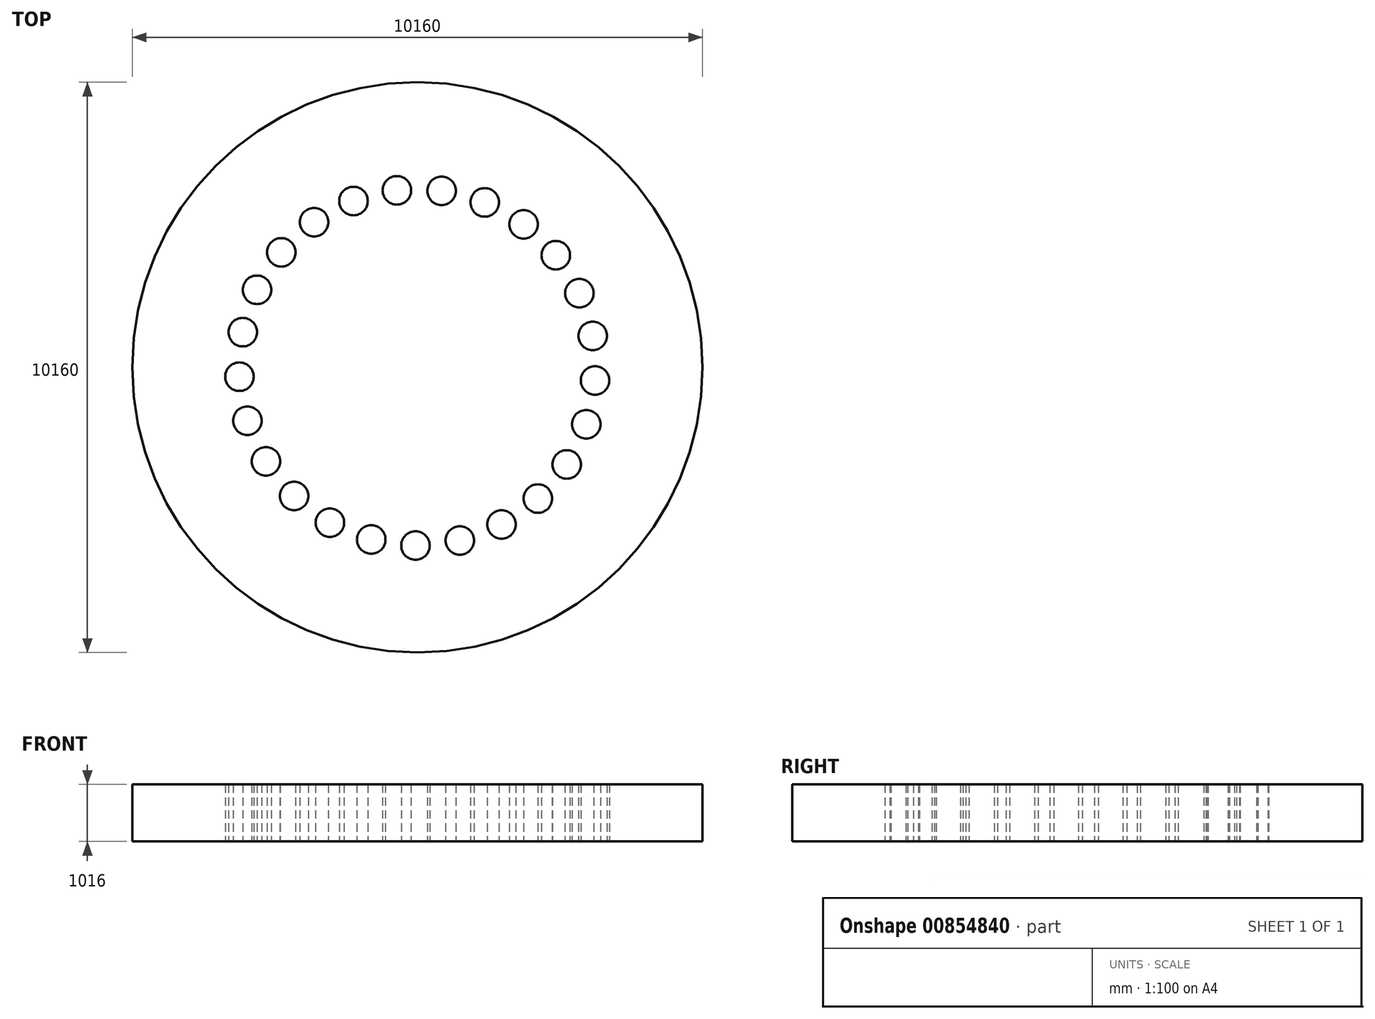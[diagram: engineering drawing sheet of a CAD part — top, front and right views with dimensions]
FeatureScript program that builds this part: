
annotation { "Feature Type Name" : "Feature", "Feature Type Description" : "" }
export const myFeature = defineFeature(function(context is Context, id is Id, definition is map)
    precondition{}
    {
        {
            var Q0;
            Q0=qCreatedBy(makeId("Top.planeOp"),FACE);
            var sketch = newSketch(context, id + "F0", { "sketchPlane" : qUnion([Q0])});
            skCircle(sketch, "E0", {"center": v(0, 0) * mm, "radius": 3175 * mm});
            skCircle(sketch, "E1", {"center": v(0, 0) * mm, "radius": 5080 * mm});
            skLineSegment(sketch, "E2", {"start": v(0, 0) * mm, "end": v(-4434.2, 0) * mm, "construction": true});
            skLineSegment(sketch, "E3", {"start": v(0, 0) * mm, "end": v(-1010.9, -3772.75) * mm, "construction": true});
            skCircle(sketch, "E4", {"center": v(-821.75, -3066.81) * mm, "radius": 254 * mm});
            skCircle(sketch, "E5.1.0", {"center": v(-33.25, -3174.83) * mm, "radius": 254 * mm});
            skCircle(sketch, "E5.2.0", {"center": v(757.34, -3083.35) * mm, "radius": 254 * mm});
            skCircle(sketch, "E5.3.0", {"center": v(1500.35, -2798.14) * mm, "radius": 254 * mm});
            skCircle(sketch, "E5.4.0", {"center": v(2149.08, -2337.1) * mm, "radius": 254 * mm});
            skCircle(sketch, "E5.5.0", {"center": v(2662.78, -1729.23) * mm, "radius": 254 * mm});
            skCircle(sketch, "E5.6.0", {"center": v(3009.16, -1012.7) * mm, "radius": 254 * mm});
            skCircle(sketch, "E5.7.0", {"center": v(3166.47, -232.53) * mm, "radius": 254 * mm});
            skCircle(sketch, "E5.8.0", {"center": v(3124.82, 562.24) * mm, "radius": 254 * mm});
            skCircle(sketch, "E5.9.0", {"center": v(2886.82, 1321.7) * mm, "radius": 254 * mm});
            skCircle(sketch, "E5.10.0", {"center": v(2467.44, 1998.1) * mm, "radius": 254 * mm});
            skCircle(sketch, "E5.11.0", {"center": v(1893.01, 2548.95) * mm, "radius": 254 * mm});
            skCircle(sketch, "E5.12.0", {"center": v(1199.64, 2939.64) * mm, "radius": 254 * mm});
            skCircle(sketch, "E5.13.0", {"center": v(430.9, 3145.62) * mm, "radius": 254 * mm});
            skCircle(sketch, "E5.14.0", {"center": v(-364.93, 3153.96) * mm, "radius": 254 * mm});
            skCircle(sketch, "E5.15.0", {"center": v(-1137.82, 2964.12) * mm, "radius": 254 * mm});
            skCircle(sketch, "E5.16.0", {"center": v(-1839.22, 2588.03) * mm, "radius": 254 * mm});
            skCircle(sketch, "E5.17.0", {"center": v(-2425.05, 2049.33) * mm, "radius": 254 * mm});
            skCircle(sketch, "E5.18.0", {"center": v(-2858.51, 1381.86) * mm, "radius": 254 * mm});
            skCircle(sketch, "E5.19.0", {"center": v(-3112.36, 627.56) * mm, "radius": 254 * mm});
            skCircle(sketch, "E5.20.0", {"center": v(-3170.65, -166.17) * mm, "radius": 254 * mm});
            skCircle(sketch, "E5.21.0", {"center": v(-3029.71, -949.45) * mm, "radius": 254 * mm});
            skCircle(sketch, "E5.22.0", {"center": v(-2698.4, -1673.08) * mm, "radius": 254 * mm});
            skCircle(sketch, "E5.23.0", {"center": v(-2197.55, -2291.59) * mm, "radius": 254 * mm});
            skCircle(sketch, "E5.24.0", {"center": v(-1558.62, -2766.1) * mm, "radius": 254 * mm});
            skSolve(sketch);
        }
        {
            var Q0;
            Q0=makeQuery(id+"F0.imprint","IMPRINT",FACE,{"disambiguationData":[TD([[makeQuery(id+"F0.imprint","IMPRINT",EDGE,{"derivedFrom":sQuery(id+"F0.wireOp",EDGE,"oxus39hn-M2Ty-7hbW-0fkP-8sFno8TxbM2q")}),-1.0]])]});
            var Q1;
            Q1=makeQuery(id+"F0.imprint","IMPRINT",FACE,{"disambiguationData":[TD([[makeQuery(id+"F0.imprint","IMPRINT",EDGE,{"derivedFrom":sQuery(id+"F0.wireOp",EDGE,"rZGO7bVd-L0fE-PMNe-PRq9-Aw8XqQe64tch")}),1.0]])]});
            var Q2;
            Q2=makeQuery(id+"F0.imprint","IMPRINT",FACE,{"disambiguationData":[TD([[makeQuery(id+"F0.imprint","IMPRINT",EDGE,{"derivedFrom":sQuery(id+"F0.wireOp",EDGE,"E1")}),1.0]])]});
            var Q3;
            {var subQ1=sQuery(id+"F0.wireOp",EDGE,"E0");var subQ37=sQuery(id+"F0.wireOp",EDGE,"E5.8.0");var subQ38=makeQuery(id+"F0.imprint","INTERSECT",VERTEX,{"disambiguationData":[OD(0.0)],"derivedFrom":[subQ1,subQ37]});Q3=makeQuery(id+"F0.imprint","IMPRINT",FACE,{"disambiguationData":[TD([[makeQuery(id+"F0.imprint","IMPRINT",EDGE,{"disambiguationData":[TD([[subQ38,1.0]])],"derivedFrom":subQ1}),1.0]])]});}
            extrude(context, id + "F1", {"entities" : qUnion([Q0, Q1, Q2, Q3]), "endBound" : BoundingType.SYMMETRIC, "depth" : 1016 * mm, "offsetDistance" : 25.4 * mm});
        }
    });
